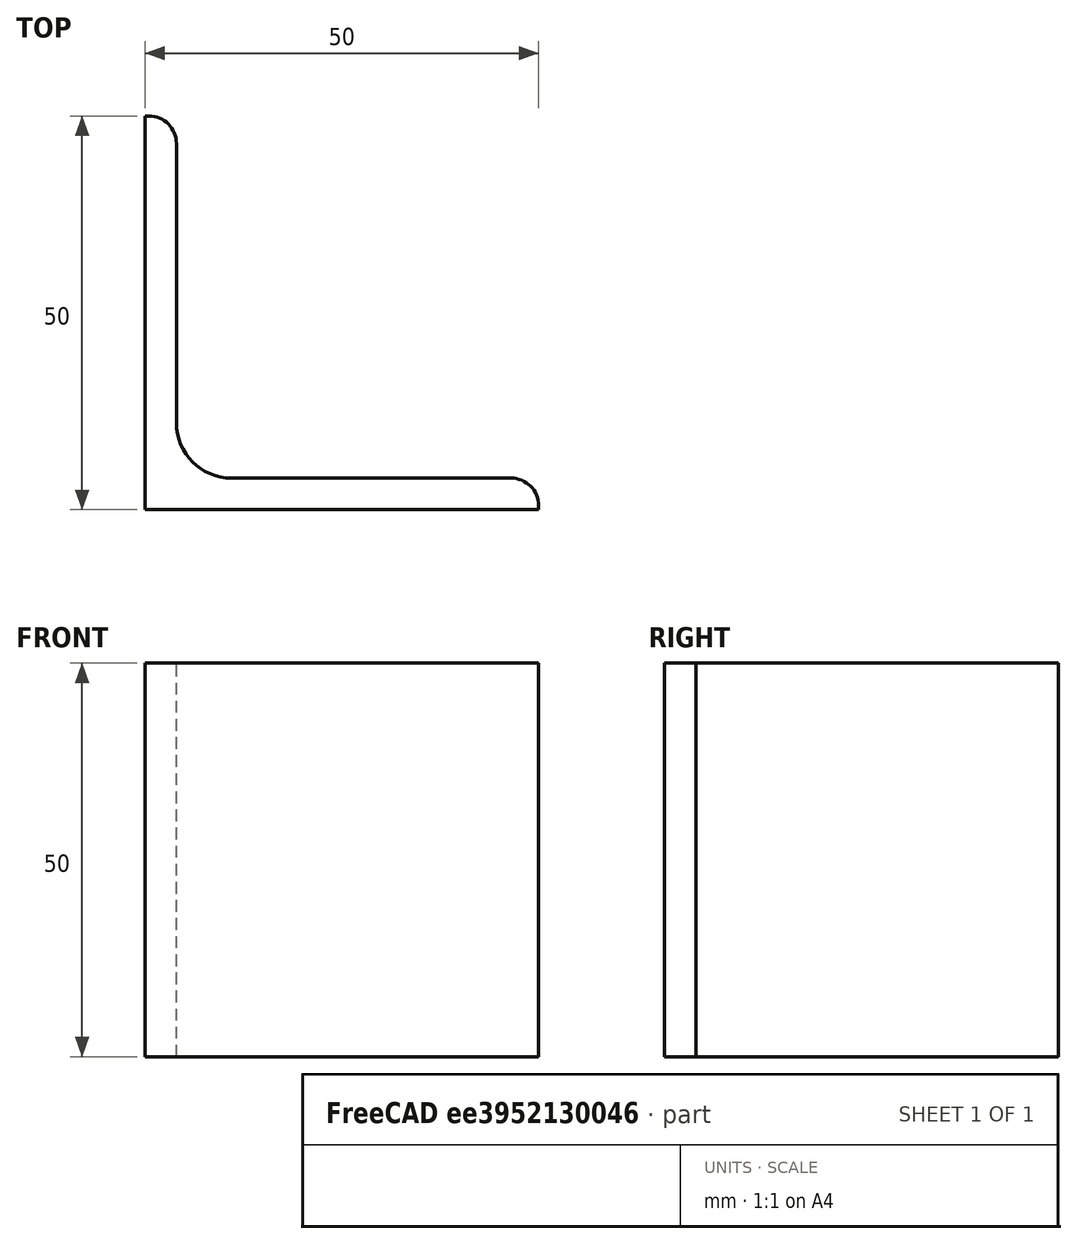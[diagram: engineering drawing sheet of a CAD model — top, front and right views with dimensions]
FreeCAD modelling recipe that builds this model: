
FCSTD DOCUMENT  (FreeCAD 0.15R4671 (Git))
Label: Angle Bar L50x50x4 EN10056 S235JR
License: All rights reserved
LicenseURL: http://en.wikipedia.org/wiki/All_rights_reserved
objects: Sketcher::SketchObject×1, Part::Extrusion×1
note: 2 computed .brp shape members not serialized (recipe doc carries the construction recipe); baked Part::Feature solids carry a one-line shape summary decoded from their .brp

FEATURE [Sketcher::SketchObject] Sketch
  sketch-geometry (9):
    g0: LineSegment StartX=0 StartY=0 StartZ=0 EndX=50 EndY=0 EndZ=0
    g1: LineSegment StartX=50 StartY=0 StartZ=0 EndX=50 EndY=0.5 EndZ=0
    g2: LineSegment StartX=46.5 StartY=4 StartZ=0 EndX=11 EndY=4 EndZ=0
    g3: LineSegment StartX=0 StartY=0 StartZ=0 EndX=0 EndY=50 EndZ=0
    g4: LineSegment StartX=0 StartY=50 StartZ=0 EndX=0.5 EndY=50 EndZ=0
    g5: LineSegment StartX=4 StartY=46.5 StartZ=0 EndX=4 EndY=11 EndZ=0
    g6: ArcOfCircle CenterX=11 CenterY=11 CenterZ=0 NormalX=0 NormalY=0 NormalZ=1 Radius=7 StartAngle=3.14159 EndAngle=4.71239
    g7: ArcOfCircle CenterX=0.5 CenterY=46.5 CenterZ=0 NormalX=0 NormalY=0 NormalZ=1 Radius=3.5 StartAngle=0 EndAngle=1.5708
    g8: ArcOfCircle CenterX=46.5 CenterY=0.5 CenterZ=0 NormalX=0 NormalY=0 NormalZ=1 Radius=3.5 StartAngle=0 EndAngle=1.5708
  constraints (23):
    c: Coincident(g0,g-1)
    c: Horizontal(g0)
    c: Coincident(g1,g0)
    c: Vertical(g1)
    c: Horizontal(g2)
    c: Coincident(g3,g-1)
    c: Vertical(g3)
    c: Coincident(g4,g3)
    c: Horizontal(g4)
    c: Vertical(g5)
    c: Tangent(g5,g6) = -1.5708
    c: Tangent(g2,g6) = 1.5708
    c: Tangent(g4,g7) = 1.5708
    c: Tangent(g5,g7) = 1.5708
    c: Tangent(g2,g8) = -1.5708
    c: Tangent(g1,g8) = -1.5708
    c: DistanceX(g0) = 50
    c: DistanceY(g3) = 50
    c: DistanceY(g0,g2) = 4
    c: DistanceX(g3,g5) = 4
    c: Radius(g6) = 7
    c: Radius(g8) = 3.5
    c: Radius(g7) = 3.5
FEATURE [Part::Extrusion] Extrude  label="Angle Bar L50x50x4 EN10056 S235JR"
  Base = -> Sketch
  Dir = (0,0,50)
  Solid = true
